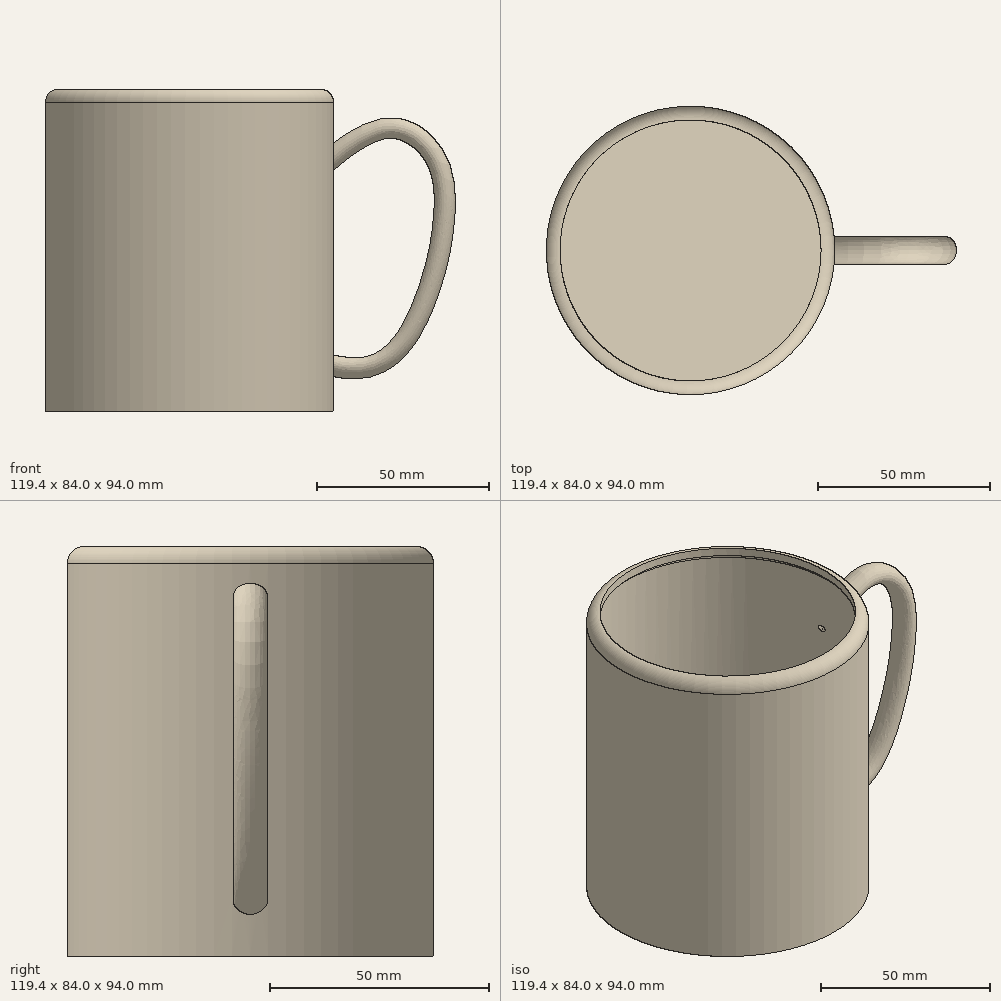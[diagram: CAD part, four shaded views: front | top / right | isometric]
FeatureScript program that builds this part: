
annotation { "Feature Type Name" : "Feature", "Feature Type Description" : "" }
export const myFeature = defineFeature(function(context is Context, id is Id, definition is map)
    precondition{}
    {
        {
            var Q0;
            Q0=qCreatedBy(makeId("Top.planeOp"),FACE);
            var sketch = newSketch(context, id + "F0", { "sketchPlane" : qUnion([Q0])});
            skCircle(sketch, "E0", {"center": v(0, 0) * mm, "radius": 42 * mm});
            skSolve(sketch);
        }
        {
            var Q0;
            Q0 = qSketchRegion(id + "F0", true);
            extrude(context, id + "F1", {"entities" : qUnion([Q0]), "depth" : 94 * mm, "offsetDistance" : 25 * mm});
        }
        {
            var Q0;
            Q0=makeQuery(id+"F1.opExtrude","CAP_EDGE",EDGE,{"disambiguationData":[OSD([sQuery(id+"F0.wireOp",EDGE,"E0")])],"isStart":false});
            fillet(context, id + "F2", {"entities" : qUnion([Q0]), "radius" : 4 * mm, "tangentPropagation" : true, "allowEdgeOverflow" : false});
        }
        {
            var Q0;
            Q0=qCreatedBy(makeId("Front.planeOp"),FACE);
            var sketch = newSketch(context, id + "F3", { "sketchPlane" : qUnion([Q0])});
            skFitSpline(sketch, "E1", {"points": [v(41.45, 74.2) * mm, v(58.86, 82.61) * mm, v(72.33, 72.76) * mm, v(74.11, 54.11) * mm, v(71.1, 39.1) * mm, v(62.59, 20.42) * mm, v(50.51, 12.74) * mm, v(36.57, 14.36) * mm, v(29.57, 19.84) * mm], "startDerivative": vector(96.25, 80.11) * mm, "endDerivative": vector(-64.68, 140.4) * mm});
            skSolve(sketch);
        }
        {
            var Q0;
            Q0=qCreatedBy(makeId("Right.planeOp"),FACE);
            cPlane(context, id + "F4", {"entities" : qUnion([Q0]), "cplaneType" : CPlaneType.OFFSET, "offset" : 42 * mm, "width" : 150 * mm, "height" : 150 * mm});
        }
        {
            var Q0;
            Q0=qCreatedBy(id+"F4.planeOp",FACE);
            var sketch = newSketch(context, id + "F5", { "sketchPlane" : qUnion([Q0])});
            skCircle(sketch, "E2", {"center": v(0, 74.3) * mm, "radius": 4 * mm});
            skSolve(sketch);
        }
        {
            var Q0;
            Q0=makeQuery(id+"F5.imprint","IMPRINT",FACE,{"disambiguationData":[TD([[makeQuery(id+"F5.imprint","IMPRINT",EDGE,{"derivedFrom":sQuery(id+"F5.wireOp",EDGE,"E2")}),1.0]])]});
            var Q1;
            Q1=sQuery(id+"F3.wireOp",EDGE,"E1");
            sweep(context, id + "F6", {"operationType" : NewBodyOperationType.ADD, "profiles" : qUnion([Q0]), "path" : qUnion([Q1])});
        }
        {
            var Q0;
            Q0=makeQuery(id+"F1.opExtrude","CAP_FACE",FACE,{"disambiguationData":[OSD([sQuery(id+"F0.wireOp",EDGE,"E0")])],"isStart":false});
            shell(context, id + "F7", {"entities" : qUnion([Q0]), "thickness" : 2.5 * mm});
        }
    });
